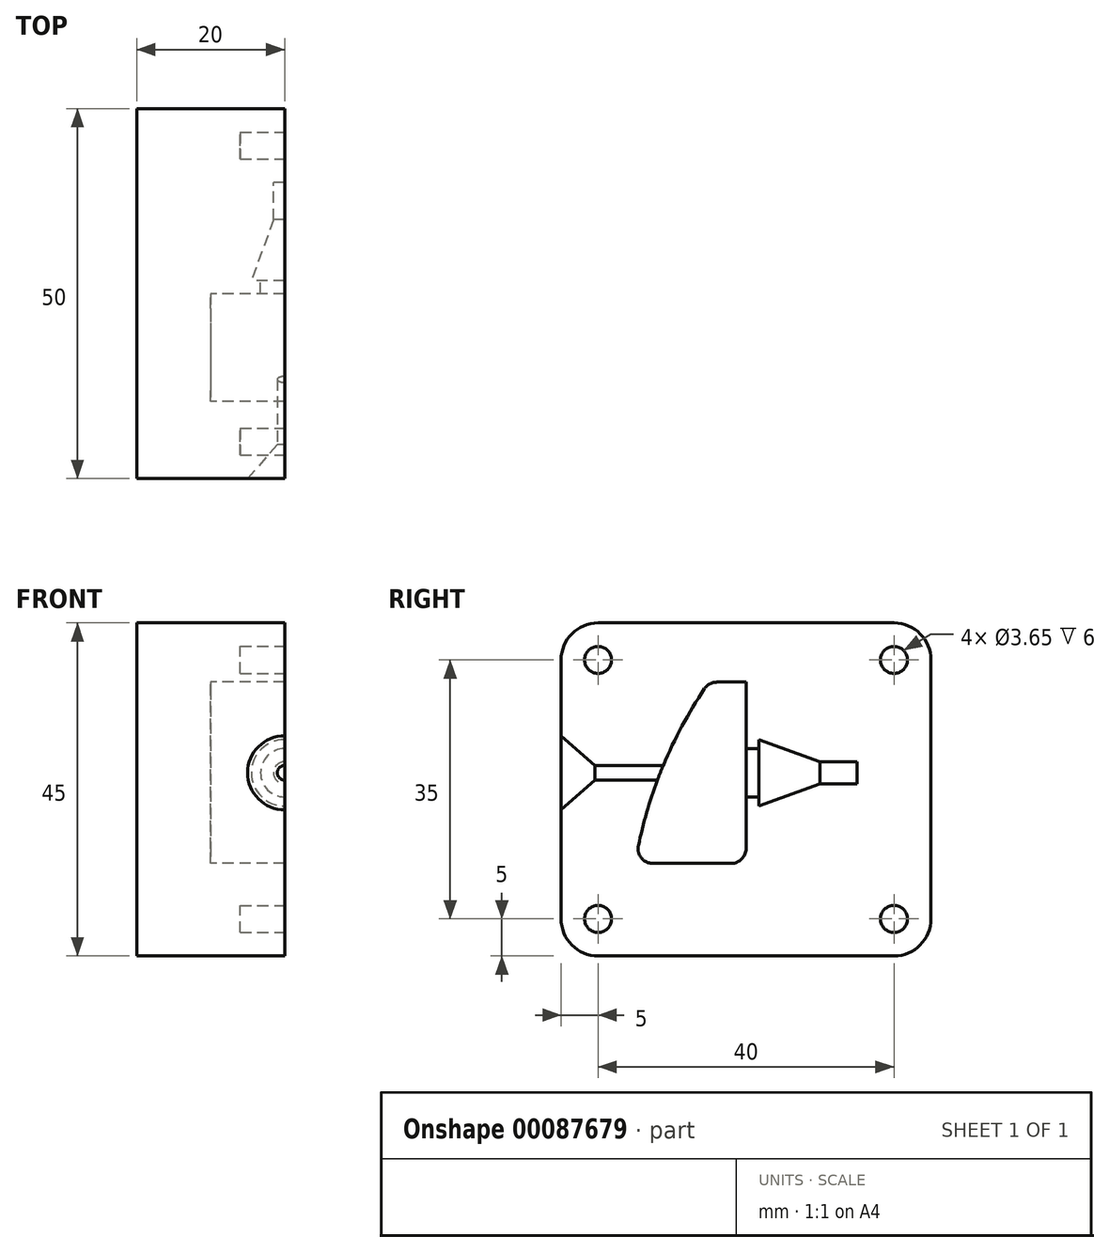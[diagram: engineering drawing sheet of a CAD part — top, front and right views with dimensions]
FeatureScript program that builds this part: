
annotation { "Feature Type Name" : "Feature", "Feature Type Description" : "" }
export const myFeature = defineFeature(function(context is Context, id is Id, definition is map)
    precondition{}
    {
        {
            var Q0;
            Q0=qCreatedBy(makeId("Right.planeOp"),FACE);
            var sketch = newSketch(context, id + "F0", { "sketchPlane" : qUnion([Q0])});
            skPoint(sketch, "E0.middle", {"position": v(0, 0) * mm});
            skLineSegment(sketch, "E1", {"start": v(0, 0) * mm, "end": v(-15, 0) * mm});
            skLineSegment(sketch, "E2", {"start": v(0, 0) * mm, "end": v(0, 24.5) * mm});
            skLineSegment(sketch, "E3", {"start": v(0, 24.5) * mm, "end": v(-5, 24.5) * mm});
            skArc(sketch, "E4", {"start": v(-5, 24.5) * mm, "mid": v(-11.37, 12.8) * mm, "end": v(-15, 0) * mm});
            skPoint(sketch, "E4.third.point", {"position": v(95.24, 21.65) * mm});
            skSolve(sketch);
        }
        {
            var Q0;
            Q0=qSketchRegion(id+"F0",true);
            extrude(context, id + "F1", {"entities" : qUnion([Q0]), "endBound" : BoundingType.SYMMETRIC, "depth" : 20 * mm});
        }
        {
            var Q0;
            Q0=makeQuery(id+"F1.opExtrude","SWEPT_FACE",FACE,{"disambiguationData":[OSD([sQuery(id+"F0.wireOp",EDGE,"E2")])]});
            var sketch = newSketch(context, id + "F2", { "sketchPlane" : qUnion([Q0])});
            skPoint(sketch, "E5", {"position": v(0, 12.25) * mm});
            skPoint(sketch, "E5.positionSnap0", {"position": v(-10, 12.25) * mm});
            skPoint(sketch, "E5.positionSnap1", {"position": v(0, 24.5) * mm});
            skSolve(sketch);
        }
        {
            var Q0;
            Q0=qCreatedBy(makeId("Right.planeOp"),FACE);
            var sketch = newSketch(context, id + "F3", { "sketchPlane" : qUnion([Q0])});
            skLineSegment(sketch, "E6", {"start": v(15, 12.25) * mm, "end": v(0, 12.25) * mm});
            skLineSegment(sketch, "E7", {"start": v(0, 15.5) * mm, "end": v(1.75, 15.5) * mm});
            skLineSegment(sketch, "E8", {"start": v(1.75, 15.5) * mm, "end": v(1.75, 16.75) * mm});
            skLineSegment(sketch, "E9", {"start": v(1.75, 16.75) * mm, "end": v(10, 13.75) * mm});
            skLineSegment(sketch, "E10", {"start": v(10, 13.75) * mm, "end": v(15, 13.75) * mm});
            skLineSegment(sketch, "E11", {"start": v(0, 15.5) * mm, "end": v(0, 12.25) * mm});
            skLineSegment(sketch, "E12", {"start": v(15, 13.75) * mm, "end": v(15, 12.25) * mm});
            skSolve(sketch);
        }
        {
            var Q0;
            Q0=makeQuery(id+"F3.imprint","IMPRINT",FACE,{"disambiguationData":[TD([[makeQuery(id+"F3.imprint","IMPRINT",EDGE,{"derivedFrom":sQuery(id+"F3.wireOp",EDGE,"E6")}),-1.0]])]});
            var Q1;
            Q1=sQuery(id+"F3.wireOp",EDGE,"E6");
            revolve(context, id + "F4", {"operationType" : NewBodyOperationType.ADD, "entities" : qUnion([Q0]), "axis" : qUnion([Q1]), "revolveType" : RevolveType.FULL});
        }
        {
            var Q0;
            Q0=makeQuery(id+"F1.opExtrude","SWEPT_EDGE",EDGE,{"disambiguationData":[OSD([sQuery(id+"F0.wireOp",EDGE,"E3"),sQuery(id+"F0.wireOp",EDGE,"E4")])]});
            var Q1;
            Q1=makeQuery(id+"F1.opExtrude","SWEPT_EDGE",EDGE,{"disambiguationData":[OSD([sQuery(id+"F0.wireOp",EDGE,"E1"),sQuery(id+"F0.wireOp",EDGE,"E4")])]});
            var Q2;
            Q2=makeQuery(id+"F1.opExtrude","SWEPT_EDGE",EDGE,{"disambiguationData":[OSD([sQuery(id+"F0.wireOp",EDGE,"E1"),sQuery(id+"F0.wireOp",EDGE,"E2")])]});
            fillet(context, id + "F5", {"entities" : qUnion([Q0, Q1, Q2]), "radius" : 2 * mm, "tangentPropagation" : true, "allowEdgeOverflow" : false});
        }
        {
            var Q0;
            Q0=qCreatedBy(makeId("Right.planeOp"),FACE);
            var sketch = newSketch(context, id + "F6", { "sketchPlane" : qUnion([Q0])});
            skLineSegment(sketch, "E13.top", {"start": v(25, 32.5) * mm, "end": v(-25, 32.5) * mm});
            skLineSegment(sketch, "E13.left", {"start": v(25, -12.5) * mm, "end": v(25, 32.5) * mm});
            skLineSegment(sketch, "E13.right", {"start": v(-25, -12.5) * mm, "end": v(-25, 32.5) * mm});
            skPoint(sketch, "E13.middle", {"position": v(0, 0) * mm});
            skLineSegment(sketch, "E14", {"start": v(-25, -12.5) * mm, "end": v(25, -12.5) * mm});
            skPoint(sketch, "E13.bottom.start.orphan", {"position": v(25, -32.5) * mm});
            skPoint(sketch, "E15.orphan", {"position": v(-25, -32.5) * mm});
            skSolve(sketch);
        }
        {
            var Q0;
            Q0=qSketchRegion(id+"F6",true);
            extrude(context, id + "F7", {"entities" : qUnion([Q0]), "depth" : 20 * mm});
        }
        {
            var Q0;
            Q0=makeQuery(id+"F1.opExtrude","SWEPT_BODY",BODY,{"disambiguationData":[OSD([sQuery(id+"F0.wireOp",EDGE,"E1"),sQuery(id+"F0.wireOp",EDGE,"E2"),sQuery(id+"F0.wireOp",EDGE,"E3"),sQuery(id+"F0.wireOp",EDGE,"E4")])]});
            var Q1;
            Q1=makeQuery(id+"F7.opExtrude","SWEPT_BODY",BODY,{"disambiguationData":[OSD([sQuery(id+"F6.wireOp",EDGE,"E13.bottom"),sQuery(id+"F6.wireOp",EDGE,"E13.top"),sQuery(id+"F6.wireOp",EDGE,"E13.left"),sQuery(id+"F6.wireOp",EDGE,"E13.right")])]});
            booleanBodies(context, id + "F8", {"operationType" : BooleanOperationType.SUBTRACTION, "tools" : qUnion([Q0]), "targets" : qUnion([Q1])});
        }
        {
            var Q0;
            {var subQ0=makeQuery(id+"F7.opExtrude","SWEPT_FACE",FACE,{"disambiguationData":[OSD([sQuery(id+"F6.wireOp",EDGE,"E13.right")])]});Q0=makeQuery(id+"F3Q9CtZ0ULCDG1u_2.boolean.opBoolean","MERGE",FACE,{"derivedFrom":[subQ0,makeQuery(id+"F3Q9CtZ0ULCDG1u_2.opPattern","COPY",FACE,{"derivedFrom":subQ0,"instanceName":"1"})]});}
            var sketch = newSketch(context, id + "F9", { "sketchPlane" : qUnion([Q0])});
            skPoint(sketch, "E16", {"position": v(0, 12.25) * mm});
            skSolve(sketch);
        }
        {
            var Q0;
            Q0=sQuery(id+"F9.wireOp",VERTEX,"E16");
            var Q1;
            Q1=makeQuery(id+"F7.opExtrude","SWEPT_BODY",BODY,{"disambiguationData":[OSD([sQuery(id+"F6.wireOp",EDGE,"E13.top"),sQuery(id+"F6.wireOp",EDGE,"E13.left"),sQuery(id+"F6.wireOp",EDGE,"E13.right"),sQuery(id+"F6.wireOp",EDGE,"E14")])]});
            hole(context, id + "F10", {"style" : HoleStyle.C_SINK, "endStyle" : HoleEndStyle.BLIND, "holeDiameter" : 2 * mm, "cSinkDiameter" : 10 * mm, "cSinkAngle" : 82 * degree, "holeDepth" : 20 * mm, "locations" : qUnion([Q0]), "scope" : qUnion([Q1])});
        }
        {
            var Q0;
            Q0=makeQuery(id+"F7.opExtrude","SWEPT_EDGE",EDGE,{"disambiguationData":[OSD([sQuery(id+"F6.wireOp",EDGE,"E13.top"),sQuery(id+"F6.wireOp",EDGE,"E13.right")])]});
            var Q1;
            Q1=makeQuery(id+"F7.opExtrude","SWEPT_EDGE",EDGE,{"disambiguationData":[OSD([sQuery(id+"F6.wireOp",EDGE,"E13.top"),sQuery(id+"F6.wireOp",EDGE,"E13.left")])]});
            var Q2;
            Q2=makeQuery(id+"F7.opExtrude","SWEPT_EDGE",EDGE,{"disambiguationData":[OSD([sQuery(id+"F6.wireOp",EDGE,"E13.right"),sQuery(id+"F6.wireOp",EDGE,"E14")])]});
            var Q3;
            Q3=makeQuery(id+"F7.opExtrude","SWEPT_EDGE",EDGE,{"disambiguationData":[OSD([sQuery(id+"F6.wireOp",EDGE,"E13.left"),sQuery(id+"F6.wireOp",EDGE,"E14")])]});
            fillet(context, id + "F11", {"entities" : qUnion([Q0, Q1, Q2, Q3]), "radius" : 5 * mm, "tangentPropagation" : true, "allowEdgeOverflow" : false});
        }
        {
            var Q0;
            Q0=makeQuery(id+"F6.imprint","IMPRINT",FACE,{"disambiguationData":[TD([[makeQuery(id+"F6.imprint","IMPRINT",EDGE,{"derivedFrom":sQuery(id+"F6.wireOp",EDGE,"E13.top")}),1.0]])]});
            var sketch = newSketch(context, id + "F12", { "sketchPlane" : qUnion([Q0])});
            skLineSegment(sketch, "E17.bottom", {"start": v(-20, -7.5) * mm, "end": v(20, -7.5) * mm, "construction": true});
            skLineSegment(sketch, "E17.top", {"start": v(-20, 27.5) * mm, "end": v(20, 27.5) * mm, "construction": true});
            skLineSegment(sketch, "E17.left", {"start": v(-20, -7.5) * mm, "end": v(-20, 27.5) * mm, "construction": true});
            skLineSegment(sketch, "E17.right", {"start": v(20, -7.5) * mm, "end": v(20, 27.5) * mm, "construction": true});
            skPoint(sketch, "E17.middle", {"position": v(0, 10) * mm});
            skCircle(sketch, "E18", {"center": v(20, 27.5) * mm, "radius": 1.75 * mm});
            skCircle(sketch, "E19", {"center": v(-20, 27.5) * mm, "radius": 1.75 * mm});
            skCircle(sketch, "E20", {"center": v(-20, -7.5) * mm, "radius": 1.75 * mm});
            skCircle(sketch, "E21", {"center": v(20, -7.5) * mm, "radius": 1.75 * mm});
            skSolve(sketch);
        }
        {
            var Q0;
            Q0=qSketchRegion(id+"F12",true);
            extrude(context, id + "F13", {"entities" : qUnion([Q0]), "operationType" : NewBodyOperationType.ADD, "oppositeDirection" : true, "depth" : 5 * mm});
        }
        {
            var Q0;
            Q0=makeQuery(id+"F7.opExtrude","SWEPT_BODY",BODY,{"disambiguationData":[OSD([sQuery(id+"F6.wireOp",EDGE,"E13.top"),sQuery(id+"F6.wireOp",EDGE,"E13.left"),sQuery(id+"F6.wireOp",EDGE,"E13.right"),sQuery(id+"F6.wireOp",EDGE,"E14")])]});
            var Q1;
            Q1=qCreatedBy(makeId("Right.planeOp"),FACE);
            mirror(context, id + "F14", {"operationType" : NewBodyOperationType.ADD, "entities" : qUnion([Q0]), "mirrorPlane" : qUnion([Q1])});
        }
        {
            var Q0;
            {var subQ0=makeQuery(id+"F7.opExtrude","SWEPT_FACE",FACE,{"disambiguationData":[OSD([sQuery(id+"F6.wireOp",EDGE,"E13.right")])]});Q0=makeQuery(id+"F14.boolean.opBoolean","MERGE",FACE,{"derivedFrom":[subQ0,makeQuery(id+"F14.opPattern","COPY",FACE,{"derivedFrom":subQ0,"instanceName":"1"})]});}
            var sketch = newSketch(context, id + "F15", { "sketchPlane" : qUnion([Q0])});
            skLineSegment(sketch, "E22", {"start": v(0, -48.56) * mm, "end": v(0, 51.63) * mm});
            skLineSegment(sketch, "E23", {"start": v(0, 51.63) * mm, "end": v(33.08, 51.63) * mm});
            skLineSegment(sketch, "E24", {"start": v(33.08, 51.63) * mm, "end": v(33.08, -48.56) * mm});
            skLineSegment(sketch, "E25", {"start": v(0, -48.56) * mm, "end": v(33.08, -48.56) * mm});
            skSolve(sketch);
        }
        {
            var Q0;
            Q0 = qSketchRegion(id + "F15", true);
            extrude(context, id + "F16", {"entities" : qUnion([Q0]), "operationType" : NewBodyOperationType.REMOVE, "endBound" : BoundingType.THROUGH_ALL, "oppositeDirection" : true, "depth" : 25 * mm});
        }
        {
            var Q0;
            Q0=makeQuery(id+"F6.imprint","IMPRINT",FACE,{"disambiguationData":[TD([[makeQuery(id+"F6.imprint","IMPRINT",EDGE,{"derivedFrom":sQuery(id+"F6.wireOp",EDGE,"E13.top")}),1.0]])]});
            var sketch = newSketch(context, id + "F17", { "sketchPlane" : qUnion([Q0])});
            skLineSegment(sketch, "E26.bottom", {"start": v(20, -7.5) * mm, "end": v(-20, -7.5) * mm, "construction": true});
            skLineSegment(sketch, "E26.top", {"start": v(20, 27.5) * mm, "end": v(-20, 27.5) * mm, "construction": true});
            skLineSegment(sketch, "E26.left", {"start": v(20, -7.5) * mm, "end": v(20, 27.5) * mm, "construction": true});
            skLineSegment(sketch, "E26.right", {"start": v(-20, -7.5) * mm, "end": v(-20, 27.5) * mm, "construction": true});
            skPoint(sketch, "E26.middle", {"position": v(0, 10) * mm});
            skCircle(sketch, "E27", {"center": v(-20, 27.5) * mm, "radius": 1.82 * mm});
            skCircle(sketch, "E28", {"center": v(20, 27.5) * mm, "radius": 1.82 * mm});
            skCircle(sketch, "E29", {"center": v(20, -7.5) * mm, "radius": 1.82 * mm});
            skCircle(sketch, "E30", {"center": v(-20, -7.5) * mm, "radius": 1.82 * mm});
            skSolve(sketch);
        }
        {
            var Q0;
            Q0 = qSketchRegion(id + "F17", true);
            extrude(context, id + "F18", {"entities" : qUnion([Q0]), "operationType" : NewBodyOperationType.REMOVE, "oppositeDirection" : true, "depth" : 6 * mm});
        }
    });
